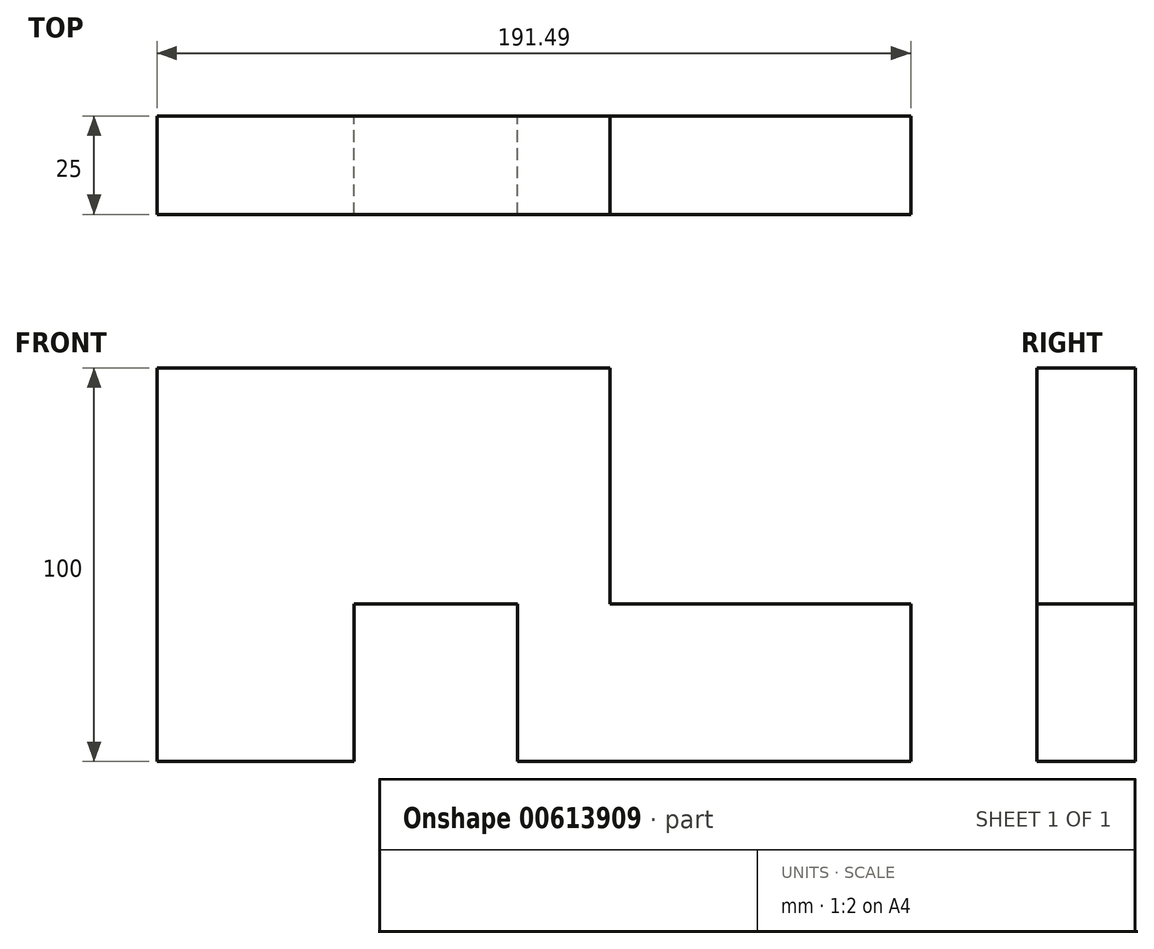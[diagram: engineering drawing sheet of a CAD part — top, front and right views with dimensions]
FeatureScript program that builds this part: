
annotation { "Feature Type Name" : "Feature", "Feature Type Description" : "" }
export const myFeature = defineFeature(function(context is Context, id is Id, definition is map)
    precondition{}
    {
        {
            var Q0;
            Q0=qCreatedBy(makeId("Front.planeOp"),FACE);
            var sketch = newSketch(context, id + "F0", { "sketchPlane" : qUnion([Q0])});
            skLineSegment(sketch, "E0", {"start": v(0, 0) * mm, "end": v(100, 0) * mm});
            skLineSegment(sketch, "E1", {"start": v(100, 0) * mm, "end": v(100, 40) * mm});
            skLineSegment(sketch, "E2", {"start": v(0, 0) * mm, "end": v(0, 40) * mm});
            skLineSegment(sketch, "E3", {"start": v(0, 40) * mm, "end": v(-41.5, 40) * mm});
            skLineSegment(sketch, "E4", {"start": v(-41.5, 40) * mm, "end": v(-41.5, 0) * mm});
            skLineSegment(sketch, "E5", {"start": v(-41.5, 0) * mm, "end": v(-91.5, 0) * mm});
            skLineSegment(sketch, "E6", {"start": v(-91.5, 0) * mm, "end": v(-91.5, 100) * mm});
            skLineSegment(sketch, "E7", {"start": v(-91.5, 100) * mm, "end": v(23.5, 100) * mm});
            skLineSegment(sketch, "E8", {"start": v(23.5, 100) * mm, "end": v(23.5, 40) * mm});
            skLineSegment(sketch, "E9", {"start": v(23.5, 40) * mm, "end": v(100, 40) * mm});
            skSolve(sketch);
        }
        {
            var Q0;
            Q0 = qSketchRegion(id + "F0", true);
            extrude(context, id + "F1", {"entities" : qUnion([Q0]), "depth" : 25 * mm, "offsetDistance" : 25 * mm});
        }
    });
